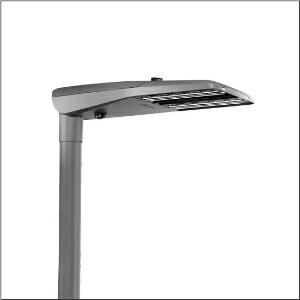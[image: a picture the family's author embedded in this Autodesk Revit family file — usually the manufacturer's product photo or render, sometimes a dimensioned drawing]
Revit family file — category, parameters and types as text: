
# Revit family: streetlight_sl_11_iq_midi___st1_2a_5xc3a11y08me_f942
name_source: partatom
category: Lighting Fixtures
units: mm (PartAtom-declared; Revit-internal decimal feet)

## family parameters
Cut with Voids When Loaded = No
Host = Face
Light Source = No
Part Type = Normal
Room Calculation Point = No
Round Connector Dimension = Use Diameter
Shared = No

## types (1)
- --- (1 x LED, 11200 lm, 123.4 W, 1800K)
    Apparent Load = 123 VA
    CIE Flux Codes = 32 70 96 100 100
    Color Rendering = 70
    Color Temperature = 1800K
    Default Elevation = 1800 mm  [stored 5.90551 ft]
    Description = Streetlight SL 11 iQ midi, mast luminaire, primary light control with 3 zone facetted reflector, of plastic, silver coated, highly specular, primary optical cover: cover, of PMMA, transparent, light distribution: ST1.2a, light emission: direct distribution, primary light characteristic: asymmetric, installation type: post-top, side-entry, LED, High Power LED, rated luminous flux: 11.200lm, luminous efficacy: 91lm/W, light colour: 718, colour temperature: 1800K, control: presetting dimming logarithmic, Street-Remote, Auto-Match, Temp-Guard, Lumen-Switch, Night-Set, Smart-Wire, Light-Fading, Desk-Remote (wireless, voltage-free reading and setting of iQ features in the workshop via application-optimized NFC function/RFID function), optimised constant luminous flux control (CLO 2.0), with cable H07RN-F 5x 1.5mm², mains connection: 230..240V, AC, 50/60Hz, connection cable pre-assembled, cable length: 12,5m, start of lifetime: 123W, end of service life: 131W, reduction: 54W, luminaire housing, of diecast aluminium, powder-coated, Siteco® metallic grey (DB 702S), please order mast flange separately, inclination adjustable without tools: 0°, 5°, 10°, 15° (post-top) | 0°, -5°, -10°, -15° (side-entry), sealing non-destructively replaceable, multi-level sealing system, length: 780mm, width: 376mm, height: 118mm, mast flange for spigot size: 42mm (side-entry): 5XC10008XM4, 60/48mm (side-entry/post-top): 5XC10108XM2, 76/60mm (side-entry/post-top): 5XC10108XM1, equipment: Power, Smart Interface below and above, protection rating (complete): IP66, insulation class (complete): insulation class II (safety insulation), certification: CE, ENEC, VDE, UKCA, impact resistance: IK09, permissible operating ambient temperature for outdoor applications: -25..+50°C, standard-compliant lighting for roads and squares, Environmental Product Declaration (EPD) tested and certified by an independent institute, packaging unit: 1 piece

Light Distribution: ST1.2a
    Height = 118 mm
    Lamp = 1 x LED
    Lamp Light Flux = 11200 lm
    Lamp Power = 123.4 W
    Lamp count = 1
    Length = 780 mm
    Luminous efficacy = 91 lm/W
    Manufacturer = Siteco
    ModVariant = No
    Model = 5XC3A11Y08ME
    Number of Poles = 1
    OnlyDefault = Yes
    Power Factor = 1
    Product Name = Streetlight SL 11 iQ midi | ST1.2a
    Product group = mast luminaire | pylon top
    ProductGroupID = 6100
    Protection Class = Protection class II
    Protection Degree = IP 66
    RLX_Detail_Level = 1
    RLX_Emergency_Light_Flux = 0 lm
    RLX_Emergency_Type = 0
    RLX_Emergency_Type_DB = No
    RlxData = <blob elided: 69697 chars, md5=bf1596bb>
    Socket = socket
    Standby Power = 0 W
    System Light Flux = 11200 lm
    System Power = 123 W
    Type Comments = factory setting: luminous flux: 100 % | dim-lin: 254 | 553 mA
    Type Image = l_1004429.jpg
    URL = http://relux.com
    VarID = @adj_061001
    Voltage = 0 V
    Weight = 0.00 kg
    Width = 376 mm

note: [stored X ft] marks values corroborated as IEEE doubles in the binary element streams (Revit-internal decimal feet)

## geometry (parser evidence)
native form markers: Blend x4, Sweep x10
no freeform markers — native parametric forms only
